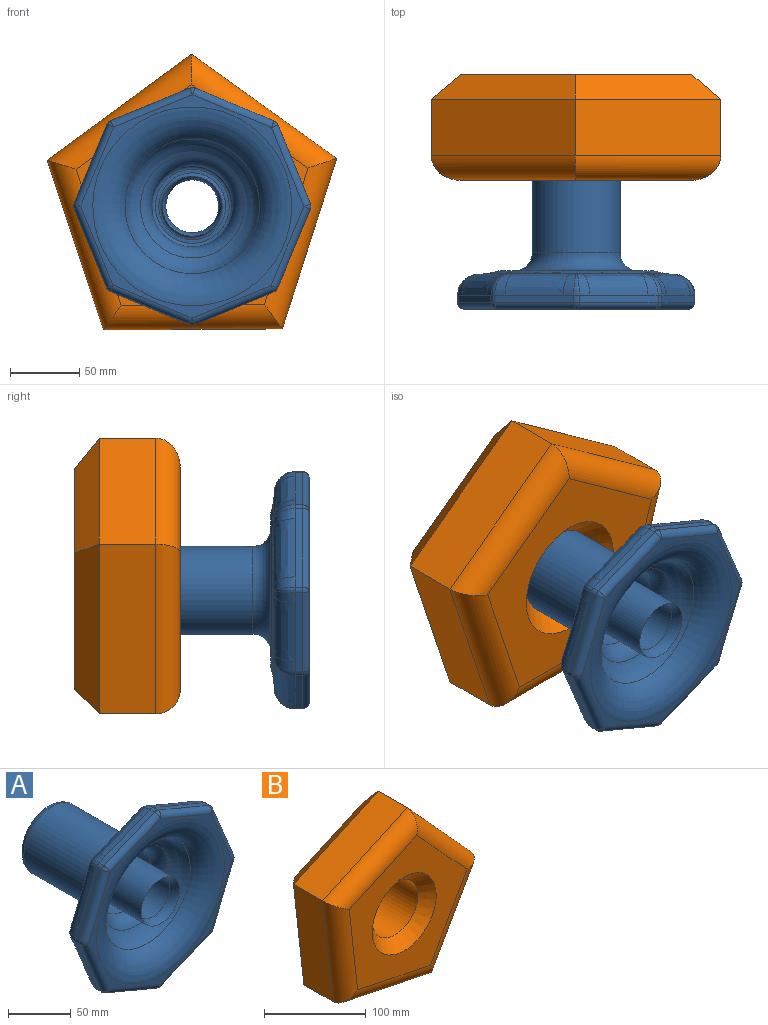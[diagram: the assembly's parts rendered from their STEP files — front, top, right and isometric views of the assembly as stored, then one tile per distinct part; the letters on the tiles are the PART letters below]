
ASSEMBLY  parts=2 mates=1
PART A: 91 faces, bbox 186.7x129.4x186.7 mm
  f0: plane 5.14x5.12mm, normal (0,1,0), area 5mm2, adj f31,f87,f88
  f1: plane 7.25x1.51mm, normal (0,1,0), area 5mm2, adj f31,f79,f83
  f2: plane 7.25x1.51mm, normal (0,1,0), area 5mm2, adj f31,f80,f84
  f3: plane 5.14x5.12mm, normal (0,1,0), area 5mm2, adj f31,f71,f75
  f4: plane 5.14x5.12mm, normal (0,1,0), area 5mm2, adj f31,f72,f76
  f5: plane 7.25x1.51mm, normal (0,1,0), area 5mm2, adj f31,f63,f67
  f6: plane 7.25x1.51mm, normal (0,1,0), area 5mm2, adj f31,f64,f68
  f7: cylinder r=31.75mm len=81.28mm, axis (0,1,0), area 16214.6mm2, adj f11,f18
  f8: cylinder r=19.05mm len=113.5mm, axis (0,1,0), area 13584.8mm2, adj f10,f90
  f9: plane 53.34x53.34mm, normal (0,1,0), area 405.4mm2, adj f10,f11
  f10: torus R=24.13mm, axis (0,-1,0), area 1047.7mm2, adj f8,f9
  f11: torus R=26.67mm, axis (0,-1,0), area 1499.3mm2, adj f7,f9
  f12: cylinder r=21.59mm len=121.92mm, axis (0,1,0), area 16538.9mm2, adj f15,f90
  f13: cylinder r=29.21mm len=81.28mm, axis (0,1,0), area 14917.5mm2, adj f16,f19
  f14: plane 53.34x53.34mm, normal (0,-1,0), area 405.4mm2, adj f15,f16
  f15: torus R=24.13mm, axis (0,-1,0), area 564.4mm2, adj f12,f14
  f16: torus R=26.67mm, axis (0,-1,0), area 709.1mm2, adj f13,f14
  f17: plane 104.72x104.72mm, normal (0,1,0), area 2405.5mm2, adj f18,f33
  f18: torus R=44.45mm, axis (0,-1,0), area 4558.1mm2, adj f7,f17
  f19: torus R=44.45mm, axis (0,-1,0), area 3320.2mm2, adj f13,f30
  f20: plane 5.14x5.12mm, normal (0,1,0), area 5mm2, adj f31,f59,f60
  f21: plane 57.06x23.49mm, normal (-0.38,0,0.92), area 318mm2, adj f47,f49,f52,f59,f61,f63
  f22: plane 56.96x23.74mm, normal (-0.92,0,0.38), area 318mm2, adj f44,f46,f49,f60,f62,f64
  f23: plane 57.06x23.49mm, normal (-0.92,0,-0.38), area 318mm2, adj f41,f43,f46,f68,f70,f72
  f24: plane 56.96x23.74mm, normal (-0.38,0,-0.92), area 318mm2, adj f38,f40,f43,f76,f78,f80
  f25: plane 57.06x23.49mm, normal (0.38,0,-0.92), area 318mm2, adj f35,f37,f40,f84,f86,f88
  f26: plane 56.96x23.74mm, normal (0.92,0,-0.38), area 318mm2, adj f34,f37,f53,f83,f85,f87
  f27: plane 57.06x23.49mm, normal (0.92,0,0.38), area 318mm2, adj f53,f55,f57,f75,f77,f79
  f28: plane 56.96x23.74mm, normal (0.38,0,0.92), area 318mm2, adj f50,f52,f57,f67,f69,f71
  f29: plane 161.25x161.25mm, normal (0,-1,0), area 2185.7mm2, adj f32,f34,f35,f38,f41,f44,f47,f50
  f30: torus R=25.4mm, axis (0,-1,0), area 4624.4mm2, adj f19,f32
  f31: torus R=68.22mm, axis (0,-1,0), area 2655.7mm2, adj f0,f1,f2,f3,f4,f5,f6,f20
  f32: torus R=71.81mm, axis (0,-1,0), area 10797.1mm2, adj f29,f30
  f33: torus R=52.36mm, axis (0,1,0), area 2856.3mm2, adj f17,f31
  f34: cylinder r=5.08mm len=58.91mm, axis (-0.38,0,-0.92), area 492.4mm2, adj f26,f29,f36,f54
  f35: cylinder r=5.08mm len=59mm, axis (-0.92,0,-0.38), area 492.4mm2, adj f25,f29,f36,f39
  f36: sphere r=5.08mm, area 20.3mm2, adj f34,f35,f37
  f37: cylinder r=5.08mm len=5.08mm, axis (0,1,0), area 20.3mm2, adj f25,f26,f36,f89
  f38: cylinder r=5.08mm len=58.91mm, axis (-0.92,0,0.38), area 492.4mm2, adj f24,f29,f39,f42
  f39: sphere r=5.08mm, area 20.3mm2, adj f35,f38,f40
  f40: cylinder r=5.08mm len=5.08mm, axis (0,1,0), area 20.3mm2, adj f24,f25,f39,f82
  f41: cylinder r=5.08mm len=59mm, axis (-0.38,0,0.92), area 492.4mm2, adj f23,f29,f42,f45
  f42: sphere r=5.08mm, area 20.3mm2, adj f38,f41,f43
  f43: cylinder r=5.08mm len=5.08mm, axis (0,1,0), area 20.3mm2, adj f23,f24,f42,f74
  f44: cylinder r=5.08mm len=58.91mm, axis (0.38,0,0.92), area 492.4mm2, adj f22,f29,f45,f48
  f45: sphere r=5.08mm, area 20.3mm2, adj f41,f44,f46
  f46: cylinder r=5.08mm len=5.08mm, axis (0,1,0), area 20.3mm2, adj f22,f23,f45,f66
  f47: cylinder r=5.08mm len=59mm, axis (0.92,0,0.38), area 492.4mm2, adj f21,f29,f48,f51
  f48: sphere r=5.08mm, area 20.3mm2, adj f44,f47,f49
  f49: cylinder r=5.08mm len=5.08mm, axis (0,1,0), area 20.3mm2, adj f21,f22,f48,f58
  f50: cylinder r=5.08mm len=58.91mm, axis (0.92,0,-0.38), area 492.4mm2, adj f28,f29,f51,f56
  f51: sphere r=5.08mm, area 20.3mm2, adj f47,f50,f52
  f52: cylinder r=5.08mm len=5.08mm, axis (0,1,0), area 20.3mm2, adj f21,f28,f51,f65
  f53: cylinder r=5.08mm len=5.08mm, axis (0,1,0), area 20.3mm2, adj f26,f27,f54,f81
  f54: sphere r=5.08mm, area 20.3mm2, adj f34,f53,f55
  f55: cylinder r=5.08mm len=59mm, axis (0.38,0,-0.92), area 492.4mm2, adj f27,f29,f54,f56
  f56: sphere r=5.08mm, area 20.3mm2, adj f50,f55,f57
  f57: cylinder r=5.08mm len=5.08mm, axis (0,1,0), area 20.3mm2, adj f27,f28,f56,f73
  f58: bspline ~17.34x12.49mm, area 61.6mm2, adj f49,f59,f60
  f59: cylinder r=15.24mm len=17.19mm, axis (-0.92,0,-0.38), area 158.1mm2, adj f20,f21,f58,f61
  f60: cylinder r=15.24mm len=17.2mm, axis (-0.38,0,-0.92), area 158.1mm2, adj f20,f22,f58,f62
  f61: bspline ~61.72x38.22mm, area 1043.9mm2, adj f21,f31,f59,f63
  f62: bspline ~61.53x37.66mm, area 1043.9mm2, adj f22,f31,f60,f64
  f63: cylinder r=15.24mm len=17.19mm, axis (-0.92,0,-0.38), area 158.1mm2, adj f5,f21,f61,f65
  f64: cylinder r=15.24mm len=17.2mm, axis (-0.38,0,-0.92), area 158.1mm2, adj f6,f22,f62,f66
  f65: bspline ~17.34x16.5mm, area 61.6mm2, adj f52,f63,f67
  f66: bspline ~17.34x16.5mm, area 61.6mm2, adj f46,f64,f68
  f67: cylinder r=15.24mm len=17.2mm, axis (-0.92,0,0.38), area 158.1mm2, adj f5,f28,f65,f69
  f68: cylinder r=15.24mm len=17.19mm, axis (0.38,0,-0.92), area 158.1mm2, adj f6,f23,f66,f70
  f69: bspline ~61.53x37.66mm, area 1043.9mm2, adj f28,f31,f67,f71
  f70: bspline ~61.72x38.22mm, area 1043.9mm2, adj f23,f31,f68,f72
  f71: cylinder r=15.24mm len=17.2mm, axis (-0.92,0,0.38), area 158.1mm2, adj f3,f28,f69,f73
  f72: cylinder r=15.24mm len=17.19mm, axis (0.38,0,-0.92), area 158.1mm2, adj f4,f23,f70,f74
  f73: bspline ~17.34x12.49mm, area 61.6mm2, adj f57,f71,f75
  f74: bspline ~17.34x12.49mm, area 61.6mm2, adj f43,f72,f76
  f75: cylinder r=15.24mm len=17.19mm, axis (-0.38,0,0.92), area 158.1mm2, adj f3,f27,f73,f77
  f76: cylinder r=15.24mm len=17.2mm, axis (0.92,0,-0.38), area 158.1mm2, adj f4,f24,f74,f78
  f77: bspline ~61.72x38.22mm, area 1043.9mm2, adj f27,f31,f75,f79
  f78: bspline ~61.53x37.66mm, area 1043.9mm2, adj f24,f31,f76,f80
  f79: cylinder r=15.24mm len=17.19mm, axis (-0.38,0,0.92), area 158.1mm2, adj f1,f27,f77,f81
  f80: cylinder r=15.24mm len=17.2mm, axis (0.92,0,-0.38), area 158.1mm2, adj f2,f24,f78,f82
  f81: bspline ~17.34x16.5mm, area 61.6mm2, adj f53,f79,f83
  f82: bspline ~17.34x16.5mm, area 61.6mm2, adj f40,f80,f84
  f83: cylinder r=15.24mm len=17.2mm, axis (0.38,0,0.92), area 158.1mm2, adj f1,f26,f81,f85
  f84: cylinder r=15.24mm len=17.19mm, axis (0.92,0,0.38), area 158.1mm2, adj f2,f25,f82,f86
  f85: bspline ~61.53x37.66mm, area 1043.9mm2, adj f26,f31,f83,f87
  f86: bspline ~61.72x38.22mm, area 1043.9mm2, adj f25,f31,f84,f88
  f87: cylinder r=15.24mm len=17.2mm, axis (0.38,0,0.92), area 158.1mm2, adj f0,f26,f85,f89
  f88: cylinder r=15.24mm len=17.19mm, axis (0.92,0,0.38), area 158.1mm2, adj f0,f25,f86,f89
  f89: bspline ~17.34x12.49mm, area 61.6mm2, adj f37,f87,f88
  f90: torus R=34.29mm, axis (0,-1,0), area 1116.4mm2, adj f8,f12
PART B: 20 faces, bbox 204.7x76.2x207.7 mm
  f0: plane 128.38x40.64mm, normal (-0.99,0,-0.11), area 5249.8mm2, adj f1,f5,f10,f18
  f1: plane 126.53x40.64mm, normal (-0.2,0,-0.98), area 5249.8mm2, adj f0,f2,f11,f19
  f2: plane 112.3x63.84mm, normal (0.87,0,-0.49), area 5249.8mm2, adj f1,f3,f13,f17
  f3: plane 95.42x87.08mm, normal (0.74,0,0.67), area 5249.8mm2, adj f2,f5,f14,f15
  f4: cylinder r=31.75mm len=63.5mm, axis (0,1,0), area 10134.1mm2, adj f8,f9
  f5: plane 117.66x53.33mm, normal (-0.41,0,0.91), area 5249.8mm2, adj f0,f3,f12,f16
  f6: plane 166.18x163.79mm, normal (0,-1,0), area 12167.3mm2, adj f8,f10,f11,f12,f13,f14
  f7: plane 166.18x163.79mm, normal (0,1,0), area 12167.3mm2, adj f9,f15,f16,f17,f18,f19
  f8: cone r=31.75mm half-angle=45deg, axis (0,-1,0), area 4299.6mm2, adj f4,f6
  f9: cone r=44.45mm half-angle=45deg, axis (0,1,0), area 4299.6mm2, adj f4,f7
  f10: cylinder r=17.78mm len=130.36mm, axis (-0.11,0,0.99), area 3345.6mm2, adj f0,f6,f11,f12
  f11: cylinder r=17.78mm len=130.11mm, axis (-0.98,0,0.2), area 3345.6mm2, adj f1,f6,f10,f13
  f12: cylinder r=17.78mm len=125mm, axis (0.91,0,0.41), area 3345.6mm2, adj f5,f6,f10,f14
  f13: cylinder r=17.78mm len=121.09mm, axis (-0.49,0,-0.87), area 3345.6mm2, adj f2,f6,f11,f14
  f14: cylinder r=17.78mm len=107.4mm, axis (0.67,0,-0.74), area 3345.6mm2, adj f3,f6,f12,f13
  f15: plane 97.86x91.51mm, normal (0.52,0.71,0.48), area 2923.4mm2, adj f3,f7,f16,f17
  f16: plane 117.66x64.19mm, normal (-0.29,0.71,0.64), area 2923.4mm2, adj f5,f7,f15,f18
  f17: plane 112.3x72.91mm, normal (0.61,0.71,-0.35), area 2923.4mm2, adj f2,f7,f15,f19
  f18: plane 128.38x30.6mm, normal (-0.7,0.71,-0.08), area 2923.4mm2, adj f0,f7,f16,f19
  f19: plane 126.53x40.82mm, normal (-0.14,0.71,-0.69), area 2923.4mm2, adj f1,f7,f17,f18
PLACE A t=(-93.99,4.67,-4.39)mm fixed
PLACE B rot(axis=(0,1,0),132.1deg) t=(0.68,97.81,284.53)mm
MATE cylindrical B.f4 <-> A.f7  axis (0,1,0) through (-93.99,34.31,-4.39)mm
